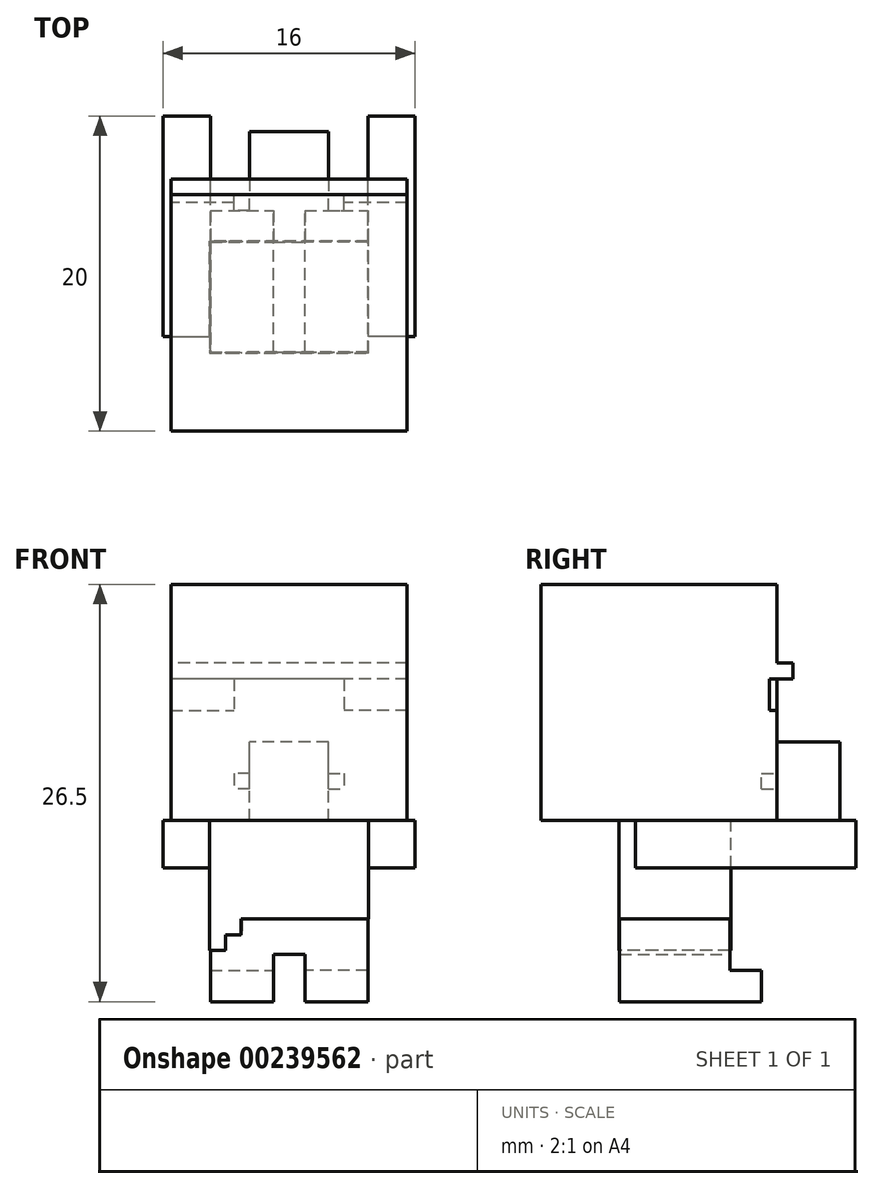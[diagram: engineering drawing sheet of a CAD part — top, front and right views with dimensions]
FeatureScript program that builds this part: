
annotation { "Feature Type Name" : "Feature", "Feature Type Description" : "" }
export const myFeature = defineFeature(function(context is Context, id is Id, definition is map)
    precondition{}
    {
        {
            var Q0;
            Q0=qCreatedBy(makeId("Front.planeOp"),FACE);
            var sketch = newSketch(context, id + "F0", { "sketchPlane" : qUnion([Q0])});
            skLineSegment(sketch, "E0.bottom", {"start": v(7.5, 7.5) * mm, "end": v(-7.5, 7.5) * mm});
            skLineSegment(sketch, "E0.top", {"start": v(7.5, -7.5) * mm, "end": v(-7.5, -7.5) * mm});
            skLineSegment(sketch, "E0.left", {"start": v(7.5, 7.5) * mm, "end": v(7.5, -7.5) * mm});
            skLineSegment(sketch, "E0.right", {"start": v(-7.5, 7.5) * mm, "end": v(-7.5, -7.5) * mm});
            skPoint(sketch, "E0.middle", {"position": v(0, 0) * mm});
            skSolve(sketch);
        }
        {
            var Q0;
            Q0 = qSketchRegion(id + "F0", true);
            extrude(context, id + "F1", {"entities" : qUnion([Q0]), "depth" : 15 * mm});
        }
        {
            var Q0;
            Q0=makeQuery(id+"F1.opExtrude","SWEPT_FACE",FACE,{"disambiguationData":[OSD([sQuery(id+"F0.wireOp",EDGE,"E0.top")])]});
            var sketch = newSketch(context, id + "F2", { "sketchPlane" : qUnion([Q0])});
            skLineSegment(sketch, "E1.bottom", {"start": v(-5, 10) * mm, "end": v(5, 10) * mm});
            skLineSegment(sketch, "E1.top", {"start": v(-5, 3) * mm, "end": v(5, 3) * mm});
            skLineSegment(sketch, "E1.left", {"start": v(-5, 10) * mm, "end": v(-5, 3) * mm});
            skLineSegment(sketch, "E1.right", {"start": v(5, 10) * mm, "end": v(5, 3) * mm});
            skSolve(sketch);
        }
        {
            var Q0;
            Q0 = qSketchRegion(id + "F2", true);
            extrude(context, id + "F3", {"entities" : qUnion([Q0]), "operationType" : NewBodyOperationType.ADD, "depth" : 8.5 * mm});
        }
        {
            var Q0;
            Q0=makeQuery(id+"F3.opExtrude","CAP_FACE",FACE,{"disambiguationData":[OSD([sQuery(id+"F2.wireOp",EDGE,"E1.bottom"),sQuery(id+"F2.wireOp",EDGE,"E1.top"),sQuery(id+"F2.wireOp",EDGE,"E1.left"),sQuery(id+"F2.wireOp",EDGE,"E1.right")])],"isStart":false});
            var sketch = newSketch(context, id + "F4", { "sketchPlane" : qUnion([Q0])});
            skLineSegment(sketch, "E2.bottom", {"start": v(-5, 10) * mm, "end": v(-1, 10) * mm});
            skLineSegment(sketch, "E2.top", {"start": v(-5, 3) * mm, "end": v(-1, 3) * mm});
            skLineSegment(sketch, "E2.left", {"start": v(-5, 10) * mm, "end": v(-5, 3) * mm});
            skLineSegment(sketch, "E2.right", {"start": v(-1, 10) * mm, "end": v(-1, 3) * mm});
            skSolve(sketch);
        }
        {
            var Q0;
            Q0 = qSketchRegion(id + "F4", true);
            extrude(context, id + "F5", {"entities" : qUnion([Q0]), "operationType" : NewBodyOperationType.ADD, "depth" : 3 * mm});
        }
        {
            var Q0;
            Q0=makeQuery(id+"F3.opExtrude","CAP_FACE",FACE,{"disambiguationData":[OSD([sQuery(id+"F2.wireOp",EDGE,"E1.bottom"),sQuery(id+"F2.wireOp",EDGE,"E1.top"),sQuery(id+"F2.wireOp",EDGE,"E1.left"),sQuery(id+"F2.wireOp",EDGE,"E1.right")])],"isStart":false});
            var sketch = newSketch(context, id + "F6", { "sketchPlane" : qUnion([Q0])});
            skLineSegment(sketch, "E3.bottom", {"start": v(5, 10) * mm, "end": v(1, 10) * mm});
            skLineSegment(sketch, "E3.top", {"start": v(5, 3) * mm, "end": v(1, 3) * mm});
            skLineSegment(sketch, "E3.left", {"start": v(5, 10) * mm, "end": v(5, 3) * mm});
            skLineSegment(sketch, "E3.right", {"start": v(1, 10) * mm, "end": v(1, 3) * mm});
            skSolve(sketch);
        }
        {
            var Q0;
            Q0 = qSketchRegion(id + "F6", true);
            extrude(context, id + "F7", {"entities" : qUnion([Q0]), "operationType" : NewBodyOperationType.ADD, "depth" : 3 * mm});
        }
        {
            var Q0;
            Q0=makeQuery(id+"F7.boolean.opBoolean","MERGE",FACE,{"derivedFrom":[makeQuery(id+"F5.boolean.opBoolean","MERGE",FACE,{"derivedFrom":[makeQuery(id+"F3.opExtrude","SWEPT_FACE",FACE,{"disambiguationData":[OSD([sQuery(id+"F2.wireOp",EDGE,"E1.top")])]}),makeQuery(id+"F5.opExtrude","SWEPT_FACE",FACE,{"disambiguationData":[OSD([sQuery(id+"F4.wireOp",EDGE,"E2.top")])]})]}),makeQuery(id+"F7.opExtrude","SWEPT_FACE",FACE,{"disambiguationData":[OSD([sQuery(id+"F6.wireOp",EDGE,"E3.top")])]})]});
            var sketch = newSketch(context, id + "F8", { "sketchPlane" : qUnion([Q0])});
            skLineSegment(sketch, "E4.bottom", {"start": v(-5, -19) * mm, "end": v(-1, -19) * mm});
            skLineSegment(sketch, "E4.top", {"start": v(-5, -17) * mm, "end": v(-1, -17) * mm});
            skLineSegment(sketch, "E4.left", {"start": v(-5, -19) * mm, "end": v(-5, -17) * mm});
            skLineSegment(sketch, "E4.right", {"start": v(-1, -19) * mm, "end": v(-1, -17) * mm});
            skSolve(sketch);
        }
        {
            var Q0;
            Q0 = qSketchRegion(id + "F8", true);
            extrude(context, id + "F9", {"entities" : qUnion([Q0]), "operationType" : NewBodyOperationType.ADD, "depth" : 2 * mm});
        }
        {
            var Q0;
            Q0=makeQuery(id+"F7.boolean.opBoolean","MERGE",FACE,{"derivedFrom":[makeQuery(id+"F5.boolean.opBoolean","MERGE",FACE,{"derivedFrom":[makeQuery(id+"F3.opExtrude","SWEPT_FACE",FACE,{"disambiguationData":[OSD([sQuery(id+"F2.wireOp",EDGE,"E1.top")])]}),makeQuery(id+"F5.opExtrude","SWEPT_FACE",FACE,{"disambiguationData":[OSD([sQuery(id+"F4.wireOp",EDGE,"E2.top")])]})]}),makeQuery(id+"F7.opExtrude","SWEPT_FACE",FACE,{"disambiguationData":[OSD([sQuery(id+"F6.wireOp",EDGE,"E3.top")])]})]});
            var sketch = newSketch(context, id + "F10", { "sketchPlane" : qUnion([Q0])});
            skLineSegment(sketch, "E5.bottom", {"start": v(5, -19) * mm, "end": v(1, -19) * mm});
            skLineSegment(sketch, "E5.top", {"start": v(5, -17) * mm, "end": v(1, -17) * mm});
            skLineSegment(sketch, "E5.left", {"start": v(5, -19) * mm, "end": v(5, -17) * mm});
            skLineSegment(sketch, "E5.right", {"start": v(1, -19) * mm, "end": v(1, -17) * mm});
            skSolve(sketch);
        }
        {
            var Q0;
            Q0 = qSketchRegion(id + "F10", true);
            extrude(context, id + "F11", {"entities" : qUnion([Q0]), "operationType" : NewBodyOperationType.ADD, "endBound" : BoundingType.SYMMETRIC, "depth" : 4 * mm});
        }
        {
            var Q0;
            Q0=makeQuery(id+"F9.boolean.opBoolean","MERGE",FACE,{"derivedFrom":[makeQuery(id+"F7.boolean.opBoolean","MERGE",FACE,{"derivedFrom":[makeQuery(id+"F3.opExtrude","SWEPT_FACE",FACE,{"disambiguationData":[OSD([sQuery(id+"F2.wireOp",EDGE,"E1.right")])]}),makeQuery(id+"F7.opExtrude","SWEPT_FACE",FACE,{"disambiguationData":[OSD([sQuery(id+"F6.wireOp",EDGE,"E3.left")])]})]}),makeQuery(id+"F9.opExtrude","SWEPT_FACE",FACE,{"disambiguationData":[OSD([sQuery(id+"F8.wireOp",EDGE,"E4.left")])]})]});
            var sketch = newSketch(context, id + "F12", { "sketchPlane" : qUnion([Q0])});
            skLineSegment(sketch, "E6.bottom", {"start": v(-9, -7.5) * mm, "end": v(5, -7.5) * mm});
            skLineSegment(sketch, "E6.top", {"start": v(-9, -10.5) * mm, "end": v(5, -10.5) * mm});
            skLineSegment(sketch, "E6.left", {"start": v(-9, -7.5) * mm, "end": v(-9, -10.5) * mm});
            skLineSegment(sketch, "E6.right", {"start": v(5, -7.5) * mm, "end": v(5, -10.5) * mm});
            skSolve(sketch);
        }
        {
            var Q0;
            Q0 = qSketchRegion(id + "F12", true);
            extrude(context, id + "F13", {"entities" : qUnion([Q0]), "operationType" : NewBodyOperationType.ADD, "depth" : 3 * mm});
        }
        {
            var Q0;
            Q0=makeQuery(id+"F11.boolean.opBoolean","MERGE",FACE,{"derivedFrom":[makeQuery(id+"F5.boolean.opBoolean","MERGE",FACE,{"derivedFrom":[makeQuery(id+"F3.opExtrude","SWEPT_FACE",FACE,{"disambiguationData":[OSD([sQuery(id+"F2.wireOp",EDGE,"E1.left")])]}),makeQuery(id+"F5.opExtrude","SWEPT_FACE",FACE,{"disambiguationData":[OSD([sQuery(id+"F4.wireOp",EDGE,"E2.left")])]})]}),makeQuery(id+"F11.opExtrude","SWEPT_FACE",FACE,{"disambiguationData":[OSD([sQuery(id+"F10.wireOp",EDGE,"E5.left")])]})]});
            var sketch = newSketch(context, id + "F14", { "sketchPlane" : qUnion([Q0])});
            skLineSegment(sketch, "E7.bottom", {"start": v(9, -7.5) * mm, "end": v(-5, -7.5) * mm});
            skLineSegment(sketch, "E7.top", {"start": v(9, -10.5) * mm, "end": v(-5, -10.5) * mm});
            skLineSegment(sketch, "E7.left", {"start": v(9, -7.5) * mm, "end": v(9, -10.5) * mm});
            skLineSegment(sketch, "E7.right", {"start": v(-5, -7.5) * mm, "end": v(-5, -10.5) * mm});
            skSolve(sketch);
        }
        {
            var Q0;
            Q0 = qSketchRegion(id + "F14", true);
            extrude(context, id + "F15", {"entities" : qUnion([Q0]), "operationType" : NewBodyOperationType.ADD, "depth" : 3 * mm});
        }
        {
            var Q0;
            Q0=makeQuery(id+"F1.opExtrude","CAP_FACE",FACE,{"disambiguationData":[OSD([sQuery(id+"F0.wireOp",EDGE,"E0.bottom"),sQuery(id+"F0.wireOp",EDGE,"E0.top"),sQuery(id+"F0.wireOp",EDGE,"E0.left"),sQuery(id+"F0.wireOp",EDGE,"E0.right")])],"isStart":true});
            var sketch = newSketch(context, id + "F16", { "sketchPlane" : qUnion([Q0])});
            skLineSegment(sketch, "E8.bottom", {"start": v(-2.5, -7.5) * mm, "end": v(2.5, -7.5) * mm});
            skLineSegment(sketch, "E8.top", {"start": v(-2.5, -2.5) * mm, "end": v(2.5, -2.5) * mm});
            skLineSegment(sketch, "E8.left", {"start": v(-2.5, -7.5) * mm, "end": v(-2.5, -2.5) * mm});
            skLineSegment(sketch, "E8.right", {"start": v(2.5, -7.5) * mm, "end": v(2.5, -2.5) * mm});
            skSolve(sketch);
        }
        {
            var Q0;
            Q0 = qSketchRegion(id + "F16", true);
            extrude(context, id + "F17", {"entities" : qUnion([Q0]), "operationType" : NewBodyOperationType.ADD, "depth" : 4 * mm});
        }
        {
            var Q0;
            Q0=makeQuery(id+"F1.opExtrude","CAP_FACE",FACE,{"disambiguationData":[OSD([sQuery(id+"F0.wireOp",EDGE,"E0.bottom"),sQuery(id+"F0.wireOp",EDGE,"E0.top"),sQuery(id+"F0.wireOp",EDGE,"E0.left"),sQuery(id+"F0.wireOp",EDGE,"E0.right")])],"isStart":true});
            var sketch = newSketch(context, id + "F18", { "sketchPlane" : qUnion([Q0])});
            skLineSegment(sketch, "E9.bottom", {"start": v(-7.5, 2.5) * mm, "end": v(7.5, 2.5) * mm});
            skLineSegment(sketch, "E9.top", {"start": v(-7.5, 1.5) * mm, "end": v(7.5, 1.5) * mm});
            skLineSegment(sketch, "E9.left", {"start": v(-7.5, 2.5) * mm, "end": v(-7.5, 1.5) * mm});
            skLineSegment(sketch, "E9.right", {"start": v(7.5, 2.5) * mm, "end": v(7.5, 1.5) * mm});
            skSolve(sketch);
        }
        {
            var Q0;
            Q0 = qSketchRegion(id + "F18", true);
            extrude(context, id + "F19", {"entities" : qUnion([Q0]), "operationType" : NewBodyOperationType.ADD, "depth" : 1 * mm});
        }
        {
            var Q0;
            {var subQ0=sQuery(id+"F0.wireOp",EDGE,"E0.left");var subQ3=sQuery(id+"F0.wireOp",EDGE,"E0.right");var subQ4=sQuery(id+"F0.wireOp",EDGE,"E0.top");Q0=makeQuery(id+"F19.boolean.opBoolean","SPLIT",FACE,{"disambiguationData":[TD([makeQuery(id+"F1.opExtrude","SWEPT_FACE",FACE,{"disambiguationData":[OSD([subQ4])]})])],"derivedFrom":makeQuery(id+"F1.opExtrude","CAP_FACE",FACE,{"disambiguationData":[OSD([sQuery(id+"F0.wireOp",EDGE,"E0.bottom"),subQ4,subQ0,subQ3])],"isStart":true})});}
            var sketch = newSketch(context, id + "F20", { "sketchPlane" : qUnion([Q0])});
            skLineSegment(sketch, "E10.bottom", {"start": v(2.5, -4.5) * mm, "end": v(3.5, -4.5) * mm});
            skLineSegment(sketch, "E10.top", {"start": v(2.5, -5.5) * mm, "end": v(3.5, -5.5) * mm});
            skLineSegment(sketch, "E10.left", {"start": v(2.5, -4.5) * mm, "end": v(2.5, -5.5) * mm});
            skLineSegment(sketch, "E10.right", {"start": v(3.5, -4.5) * mm, "end": v(3.5, -5.5) * mm});
            skPoint(sketch, "E11", {"position": v(3.5, -5) * mm});
            skSolve(sketch);
        }
        {
            var Q0;
            Q0 = qSketchRegion(id + "F20", true);
            extrude(context, id + "F21", {"entities" : qUnion([Q0]), "operationType" : NewBodyOperationType.REMOVE, "oppositeDirection" : true, "depth" : 1 * mm});
        }
        {
            var Q0;
            {var subQ0=sQuery(id+"F0.wireOp",EDGE,"E0.left");var subQ3=sQuery(id+"F0.wireOp",EDGE,"E0.right");var subQ4=sQuery(id+"F0.wireOp",EDGE,"E0.top");Q0=makeQuery(id+"F19.boolean.opBoolean","SPLIT",FACE,{"disambiguationData":[TD([makeQuery(id+"F1.opExtrude","SWEPT_FACE",FACE,{"disambiguationData":[OSD([subQ4])]})])],"derivedFrom":makeQuery(id+"F1.opExtrude","CAP_FACE",FACE,{"disambiguationData":[OSD([sQuery(id+"F0.wireOp",EDGE,"E0.bottom"),subQ4,subQ0,subQ3])],"isStart":true})});}
            var sketch = newSketch(context, id + "F22", { "sketchPlane" : qUnion([Q0])});
            skLineSegment(sketch, "E12.bottom", {"start": v(-2.5, -4.5) * mm, "end": v(-3.5, -4.5) * mm});
            skLineSegment(sketch, "E12.top", {"start": v(-2.5, -5.5) * mm, "end": v(-3.5, -5.5) * mm});
            skLineSegment(sketch, "E12.left", {"start": v(-2.5, -4.5) * mm, "end": v(-2.5, -5.5) * mm});
            skLineSegment(sketch, "E12.right", {"start": v(-3.5, -4.5) * mm, "end": v(-3.5, -5.5) * mm});
            skPoint(sketch, "E13", {"position": v(-3.5, -5) * mm});
            skPoint(sketch, "E14", {"position": v(3.5, -5) * mm});
            skSolve(sketch);
        }
        {
            var Q0;
            Q0 = qSketchRegion(id + "F22", true);
            extrude(context, id + "F23", {"entities" : qUnion([Q0]), "operationType" : NewBodyOperationType.REMOVE, "oppositeDirection" : true, "depth" : 1 * mm});
        }
        {
            var Q0;
            {var subQ0=sQuery(id+"F0.wireOp",EDGE,"E0.left");var subQ3=sQuery(id+"F0.wireOp",EDGE,"E0.right");var subQ4=sQuery(id+"F0.wireOp",EDGE,"E0.top");Q0=makeQuery(id+"F19.boolean.opBoolean","SPLIT",FACE,{"disambiguationData":[TD([makeQuery(id+"F1.opExtrude","SWEPT_FACE",FACE,{"disambiguationData":[OSD([subQ4])]})])],"derivedFrom":makeQuery(id+"F1.opExtrude","CAP_FACE",FACE,{"disambiguationData":[OSD([sQuery(id+"F0.wireOp",EDGE,"E0.bottom"),subQ4,subQ0,subQ3])],"isStart":true})});}
            var sketch = newSketch(context, id + "F24", { "sketchPlane" : qUnion([Q0])});
            skLineSegment(sketch, "E15.bottom", {"start": v(-7.5, 1.5) * mm, "end": v(-5.5, 1.5) * mm});
            skLineSegment(sketch, "E15.top", {"start": v(-7.5, -0.5) * mm, "end": v(-5.5, -0.5) * mm});
            skLineSegment(sketch, "E15.left", {"start": v(-7.5, 1.5) * mm, "end": v(-7.5, -0.5) * mm});
            skLineSegment(sketch, "E15.right", {"start": v(-5.5, 1.5) * mm, "end": v(-5.5, -0.5) * mm});
            skSolve(sketch);
        }
        {
            var Q0;
            Q0 = qSketchRegion(id + "F24", true);
            extrude(context, id + "F25", {"entities" : qUnion([Q0]), "operationType" : NewBodyOperationType.REMOVE, "oppositeDirection" : true, "depth" : 0.5 * mm});
        }
        {
            var Q0;
            {var subQ0=sQuery(id+"F0.wireOp",EDGE,"E0.left");var subQ3=sQuery(id+"F0.wireOp",EDGE,"E0.right");var subQ4=sQuery(id+"F0.wireOp",EDGE,"E0.top");Q0=makeQuery(id+"F19.boolean.opBoolean","SPLIT",FACE,{"disambiguationData":[TD([makeQuery(id+"F1.opExtrude","SWEPT_FACE",FACE,{"disambiguationData":[OSD([subQ4])]})])],"derivedFrom":makeQuery(id+"F1.opExtrude","CAP_FACE",FACE,{"disambiguationData":[OSD([sQuery(id+"F0.wireOp",EDGE,"E0.bottom"),subQ4,subQ0,subQ3])],"isStart":true})});}
            var sketch = newSketch(context, id + "F26", { "sketchPlane" : qUnion([Q0])});
            skLineSegment(sketch, "E16.bottom", {"start": v(-5.5, 1.5) * mm, "end": v(-3.5, 1.5) * mm});
            skLineSegment(sketch, "E16.top", {"start": v(-5.5, -0.5) * mm, "end": v(-3.5, -0.5) * mm});
            skLineSegment(sketch, "E16.left", {"start": v(-5.5, 1.5) * mm, "end": v(-5.5, -0.5) * mm});
            skLineSegment(sketch, "E16.right", {"start": v(-3.5, 1.5) * mm, "end": v(-3.5, -0.5) * mm});
            skSolve(sketch);
        }
        {
            var Q0;
            Q0 = qSketchRegion(id + "F26", true);
            extrude(context, id + "F27", {"entities" : qUnion([Q0]), "operationType" : NewBodyOperationType.REMOVE, "oppositeDirection" : true, "depth" : 0.5 * mm});
        }
        {
            var Q0;
            {var subQ0=sQuery(id+"F0.wireOp",EDGE,"E0.left");var subQ3=sQuery(id+"F0.wireOp",EDGE,"E0.right");var subQ4=sQuery(id+"F0.wireOp",EDGE,"E0.top");Q0=makeQuery(id+"F19.boolean.opBoolean","SPLIT",FACE,{"disambiguationData":[TD([makeQuery(id+"F1.opExtrude","SWEPT_FACE",FACE,{"disambiguationData":[OSD([subQ4])]})])],"derivedFrom":makeQuery(id+"F1.opExtrude","CAP_FACE",FACE,{"disambiguationData":[OSD([sQuery(id+"F0.wireOp",EDGE,"E0.bottom"),subQ4,subQ0,subQ3])],"isStart":true})});}
            var sketch = newSketch(context, id + "F28", { "sketchPlane" : qUnion([Q0])});
            skLineSegment(sketch, "E17.bottom", {"start": v(7.5, 1.5) * mm, "end": v(5.5, 1.5) * mm});
            skLineSegment(sketch, "E17.top", {"start": v(7.5, -0.5) * mm, "end": v(5.5, -0.5) * mm});
            skLineSegment(sketch, "E17.left", {"start": v(7.5, 1.5) * mm, "end": v(7.5, -0.5) * mm});
            skLineSegment(sketch, "E17.right", {"start": v(5.5, 1.5) * mm, "end": v(5.5, -0.5) * mm});
            skLineSegment(sketch, "E18.bottom", {"start": v(5.5, 1.5) * mm, "end": v(3.5, 1.5) * mm});
            skLineSegment(sketch, "E18.top", {"start": v(5.5, -0.5) * mm, "end": v(3.5, -0.5) * mm});
            skLineSegment(sketch, "E18.right", {"start": v(3.5, 1.5) * mm, "end": v(3.5, -0.5) * mm});
            skSolve(sketch);
        }
        {
            var Q0;
            Q0 = qSketchRegion(id + "F28", true);
            extrude(context, id + "F29", {"entities" : qUnion([Q0]), "operationType" : NewBodyOperationType.REMOVE, "oppositeDirection" : true, "depth" : 0.5 * mm});
        }
        {
            var Q0;
            Q0=makeQuery(id+"F7.boolean.opBoolean","MERGE",FACE,{"derivedFrom":[makeQuery(id+"F5.boolean.opBoolean","MERGE",FACE,{"derivedFrom":[makeQuery(id+"F3.opExtrude","SWEPT_FACE",FACE,{"disambiguationData":[OSD([sQuery(id+"F2.wireOp",EDGE,"E1.top")])]}),makeQuery(id+"F5.opExtrude","SWEPT_FACE",FACE,{"disambiguationData":[OSD([sQuery(id+"F4.wireOp",EDGE,"E2.top")])]})]}),makeQuery(id+"F7.opExtrude","SWEPT_FACE",FACE,{"disambiguationData":[OSD([sQuery(id+"F6.wireOp",EDGE,"E3.top")])]})]});
            var sketch = newSketch(context, id + "F30", { "sketchPlane" : qUnion([Q0])});
            skLineSegment(sketch, "E19.bottom", {"start": v(-5, -7.5) * mm, "end": v(5, -7.5) * mm});
            skLineSegment(sketch, "E19.top", {"start": v(-5, -13.75) * mm, "end": v(5, -13.75) * mm});
            skLineSegment(sketch, "E19.left", {"start": v(-5, -7.5) * mm, "end": v(-5, -13.75) * mm});
            skLineSegment(sketch, "E19.right", {"start": v(5, -7.5) * mm, "end": v(5, -13.75) * mm});
            skSolve(sketch);
        }
        {
            var Q0;
            Q0 = qSketchRegion(id + "F30", true);
            extrude(context, id + "F31", {"entities" : qUnion([Q0]), "operationType" : NewBodyOperationType.ADD, "depth" : 0.05 * mm});
        }
        {
            var Q0;
            Q0=makeQuery(id+"F7.boolean.opBoolean","MERGE",FACE,{"derivedFrom":[makeQuery(id+"F5.boolean.opBoolean","MERGE",FACE,{"derivedFrom":[makeQuery(id+"F3.opExtrude","SWEPT_FACE",FACE,{"disambiguationData":[OSD([sQuery(id+"F2.wireOp",EDGE,"E1.top")])]}),makeQuery(id+"F5.opExtrude","SWEPT_FACE",FACE,{"disambiguationData":[OSD([sQuery(id+"F4.wireOp",EDGE,"E2.top")])]})]}),makeQuery(id+"F7.opExtrude","SWEPT_FACE",FACE,{"disambiguationData":[OSD([sQuery(id+"F6.wireOp",EDGE,"E3.top")])]})]});
            var sketch = newSketch(context, id + "F32", { "sketchPlane" : qUnion([Q0])});
            skLineSegment(sketch, "E20.bottom", {"start": v(3, -13.75) * mm, "end": v(5, -13.75) * mm});
            skLineSegment(sketch, "E20.top", {"start": v(3, -14.75) * mm, "end": v(5, -14.75) * mm});
            skLineSegment(sketch, "E20.left", {"start": v(3, -13.75) * mm, "end": v(3, -14.75) * mm});
            skLineSegment(sketch, "E20.right", {"start": v(5, -13.75) * mm, "end": v(5, -14.75) * mm});
            skSolve(sketch);
        }
        {
            var Q0;
            Q0 = qSketchRegion(id + "F32", true);
            extrude(context, id + "F33", {"entities" : qUnion([Q0]), "operationType" : NewBodyOperationType.ADD, "depth" : 0.05 * mm});
        }
        {
            var Q0;
            Q0=makeQuery(id+"F7.boolean.opBoolean","MERGE",FACE,{"derivedFrom":[makeQuery(id+"F5.boolean.opBoolean","MERGE",FACE,{"derivedFrom":[makeQuery(id+"F3.opExtrude","SWEPT_FACE",FACE,{"disambiguationData":[OSD([sQuery(id+"F2.wireOp",EDGE,"E1.top")])]}),makeQuery(id+"F5.opExtrude","SWEPT_FACE",FACE,{"disambiguationData":[OSD([sQuery(id+"F4.wireOp",EDGE,"E2.top")])]})]}),makeQuery(id+"F7.opExtrude","SWEPT_FACE",FACE,{"disambiguationData":[OSD([sQuery(id+"F6.wireOp",EDGE,"E3.top")])]})]});
            var sketch = newSketch(context, id + "F34", { "sketchPlane" : qUnion([Q0])});
            skLineSegment(sketch, "E21.bottom", {"start": v(4, -14.75) * mm, "end": v(5, -14.75) * mm});
            skLineSegment(sketch, "E21.top", {"start": v(4, -15.75) * mm, "end": v(5, -15.75) * mm});
            skLineSegment(sketch, "E21.left", {"start": v(4, -14.75) * mm, "end": v(4, -15.75) * mm});
            skLineSegment(sketch, "E21.right", {"start": v(5, -14.75) * mm, "end": v(5, -15.75) * mm});
            skSolve(sketch);
        }
        {
            var Q0;
            Q0 = qSketchRegion(id + "F34", true);
            extrude(context, id + "F35", {"entities" : qUnion([Q0]), "operationType" : NewBodyOperationType.ADD, "depth" : 0.05 * mm});
        }
        {
            var Q0;
            Q0=makeQuery(id+"F35.boolean.opBoolean","MERGE",FACE,{"derivedFrom":[makeQuery(id+"F33.boolean.opBoolean","MERGE",FACE,{"derivedFrom":[makeQuery(id+"F31.boolean.opBoolean","MERGE",FACE,{"derivedFrom":[makeQuery(id+"F11.boolean.opBoolean","MERGE",FACE,{"derivedFrom":[makeQuery(id+"F5.boolean.opBoolean","MERGE",FACE,{"derivedFrom":[makeQuery(id+"F3.opExtrude","SWEPT_FACE",FACE,{"disambiguationData":[OSD([sQuery(id+"F2.wireOp",EDGE,"E1.left")])]}),makeQuery(id+"F5.opExtrude","SWEPT_FACE",FACE,{"disambiguationData":[OSD([sQuery(id+"F4.wireOp",EDGE,"E2.left")])]})]}),makeQuery(id+"F11.opExtrude","SWEPT_FACE",FACE,{"disambiguationData":[OSD([sQuery(id+"F10.wireOp",EDGE,"E5.left")])]})]}),makeQuery(id+"F31.opExtrude","SWEPT_FACE",FACE,{"disambiguationData":[OSD([sQuery(id+"F30.wireOp",EDGE,"E19.right")])]})]}),makeQuery(id+"F33.opExtrude","SWEPT_FACE",FACE,{"disambiguationData":[OSD([sQuery(id+"F32.wireOp",EDGE,"E20.right")])]})]}),makeQuery(id+"F35.opExtrude","SWEPT_FACE",FACE,{"disambiguationData":[OSD([sQuery(id+"F34.wireOp",EDGE,"E21.right")])]})]});
            var sketch = newSketch(context, id + "F36", { "sketchPlane" : qUnion([Q0])});
            skLineSegment(sketch, "E22.bottom", {"start": v(2.95, -15.75) * mm, "end": v(10, -15.75) * mm});
            skLineSegment(sketch, "E22.top", {"start": v(2.95, -7.5) * mm, "end": v(10, -7.5) * mm});
            skLineSegment(sketch, "E22.left", {"start": v(2.95, -15.75) * mm, "end": v(2.95, -7.5) * mm});
            skLineSegment(sketch, "E22.right", {"start": v(10, -15.75) * mm, "end": v(10, -7.5) * mm});
            skSolve(sketch);
        }
        {
            var Q0;
            Q0 = qSketchRegion(id + "F36", true);
            extrude(context, id + "F37", {"entities" : qUnion([Q0]), "operationType" : NewBodyOperationType.ADD, "depth" : 0.05 * mm});
        }
        {
            var Q0;
            Q0=makeQuery(id+"F37.boolean.opBoolean","MERGE",FACE,{"derivedFrom":[makeQuery(id+"F7.boolean.opBoolean","MERGE",FACE,{"derivedFrom":[makeQuery(id+"F5.boolean.opBoolean","MERGE",FACE,{"derivedFrom":[makeQuery(id+"F3.opExtrude","SWEPT_FACE",FACE,{"disambiguationData":[OSD([sQuery(id+"F2.wireOp",EDGE,"E1.bottom")])]}),makeQuery(id+"F5.opExtrude","SWEPT_FACE",FACE,{"disambiguationData":[OSD([sQuery(id+"F4.wireOp",EDGE,"E2.bottom")])]})]}),makeQuery(id+"F7.opExtrude","SWEPT_FACE",FACE,{"disambiguationData":[OSD([sQuery(id+"F6.wireOp",EDGE,"E3.bottom")])]})]}),makeQuery(id+"F37.opExtrude","SWEPT_FACE",FACE,{"disambiguationData":[OSD([sQuery(id+"F36.wireOp",EDGE,"E22.right")])]})]});
            var sketch = newSketch(context, id + "F38", { "sketchPlane" : qUnion([Q0])});
            skLineSegment(sketch, "E23.bottom", {"start": v(5, -7.5) * mm, "end": v(-5.05, -7.5) * mm});
            skLineSegment(sketch, "E23.top", {"start": v(5, -13.75) * mm, "end": v(-5.05, -13.75) * mm});
            skLineSegment(sketch, "E23.left", {"start": v(5, -7.5) * mm, "end": v(5, -13.75) * mm});
            skLineSegment(sketch, "E23.right", {"start": v(-5.05, -7.5) * mm, "end": v(-5.05, -13.75) * mm});
            skLineSegment(sketch, "E24.bottom", {"start": v(-5.05, -13.75) * mm, "end": v(-3.05, -13.75) * mm});
            skLineSegment(sketch, "E24.top", {"start": v(-5.05, -14.75) * mm, "end": v(-3.05, -14.75) * mm});
            skLineSegment(sketch, "E24.left", {"start": v(-5.05, -13.75) * mm, "end": v(-5.05, -14.75) * mm});
            skLineSegment(sketch, "E24.right", {"start": v(-3.05, -13.75) * mm, "end": v(-3.05, -14.75) * mm});
            skLineSegment(sketch, "E25.bottom", {"start": v(-4.05, -14.75) * mm, "end": v(-5.05, -14.75) * mm});
            skLineSegment(sketch, "E25.top", {"start": v(-4.05, -15.75) * mm, "end": v(-5.05, -15.75) * mm});
            skLineSegment(sketch, "E25.left", {"start": v(-4.05, -14.75) * mm, "end": v(-4.05, -15.75) * mm});
            skLineSegment(sketch, "E25.right", {"start": v(-5.05, -14.75) * mm, "end": v(-5.05, -15.75) * mm});
            skSolve(sketch);
        }
        {
            var Q0;
            Q0 = qSketchRegion(id + "F38", true);
            extrude(context, id + "F39", {"entities" : qUnion([Q0]), "operationType" : NewBodyOperationType.ADD, "depth" : 0.05 * mm});
        }
        {
            var Q0;
            Q0=makeQuery(id+"F39.boolean.opBoolean","MERGE",FACE,{"derivedFrom":[makeQuery(id+"F31.boolean.opBoolean","MERGE",FACE,{"derivedFrom":[makeQuery(id+"F9.boolean.opBoolean","MERGE",FACE,{"derivedFrom":[makeQuery(id+"F7.boolean.opBoolean","MERGE",FACE,{"derivedFrom":[makeQuery(id+"F3.opExtrude","SWEPT_FACE",FACE,{"disambiguationData":[OSD([sQuery(id+"F2.wireOp",EDGE,"E1.right")])]}),makeQuery(id+"F7.opExtrude","SWEPT_FACE",FACE,{"disambiguationData":[OSD([sQuery(id+"F6.wireOp",EDGE,"E3.left")])]})]}),makeQuery(id+"F9.opExtrude","SWEPT_FACE",FACE,{"disambiguationData":[OSD([sQuery(id+"F8.wireOp",EDGE,"E4.left")])]})]}),makeQuery(id+"F31.opExtrude","SWEPT_FACE",FACE,{"disambiguationData":[OSD([sQuery(id+"F30.wireOp",EDGE,"E19.left")])]})]}),makeQuery(id+"F39.opExtrude","SWEPT_FACE",FACE,{"disambiguationData":[OSD([sQuery(id+"F38.wireOp",EDGE,"E23.left")])]})]});
            var sketch = newSketch(context, id + "F40", { "sketchPlane" : qUnion([Q0])});
            skLineSegment(sketch, "E26.bottom", {"start": v(-10.05, -7.5) * mm, "end": v(-2.95, -7.5) * mm});
            skLineSegment(sketch, "E26.top", {"start": v(-10.05, -13.75) * mm, "end": v(-2.95, -13.75) * mm});
            skLineSegment(sketch, "E26.left", {"start": v(-10.05, -7.5) * mm, "end": v(-10.05, -13.75) * mm});
            skLineSegment(sketch, "E26.right", {"start": v(-2.95, -7.5) * mm, "end": v(-2.95, -13.75) * mm});
            skSolve(sketch);
        }
        {
            var Q0;
            Q0 = qSketchRegion(id + "F40", true);
            extrude(context, id + "F41", {"entities" : qUnion([Q0]), "operationType" : NewBodyOperationType.ADD, "depth" : 0.05 * mm});
        }
    });
